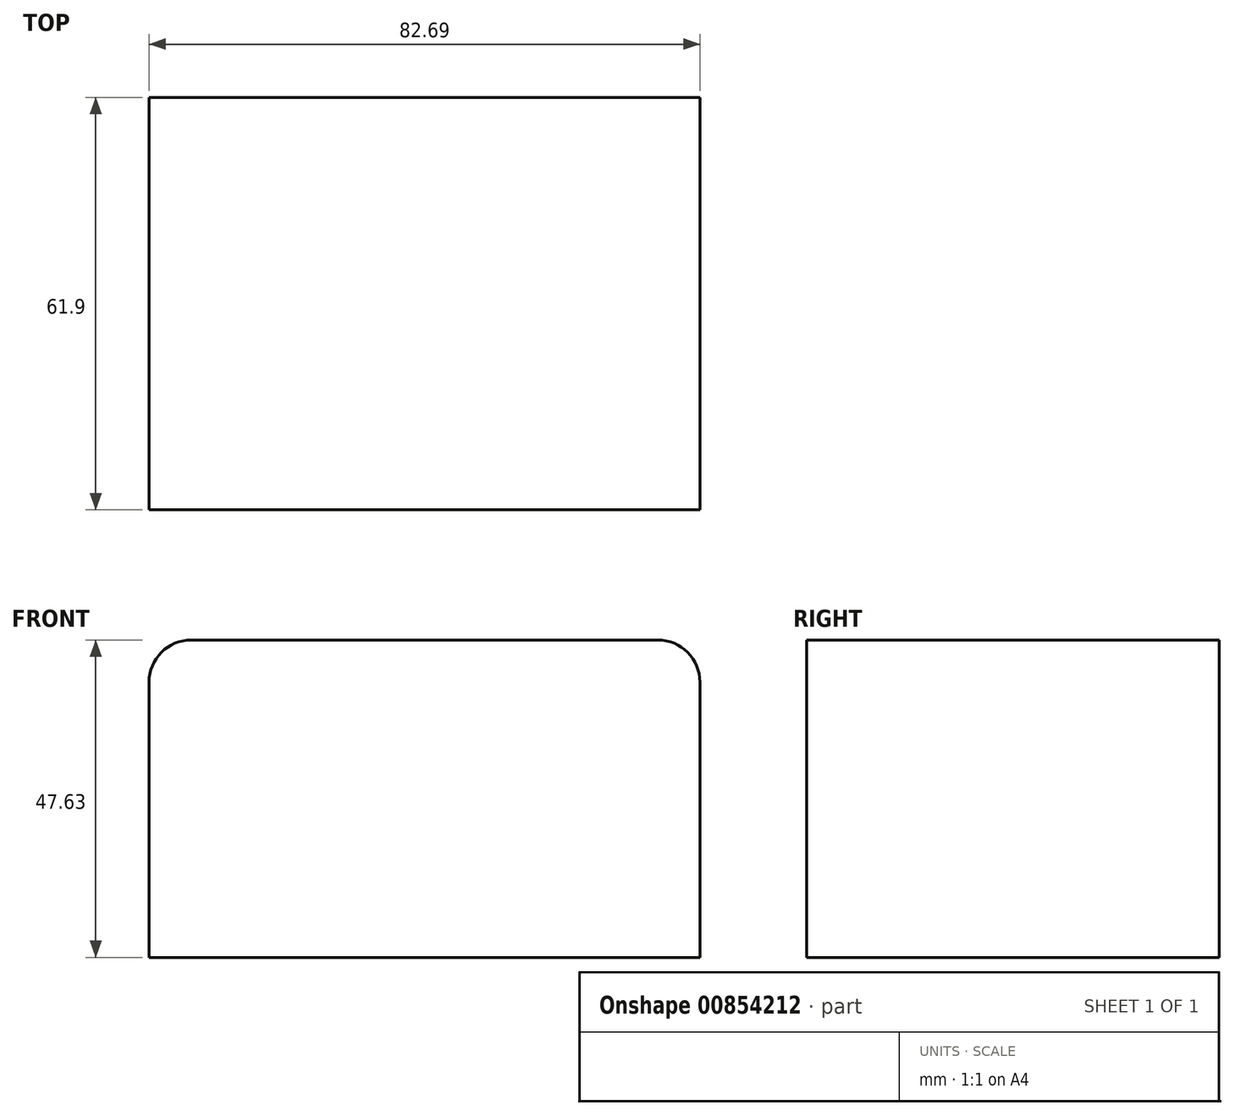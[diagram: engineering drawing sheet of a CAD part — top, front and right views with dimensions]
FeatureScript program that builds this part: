
annotation { "Feature Type Name" : "Feature", "Feature Type Description" : "" }
export const myFeature = defineFeature(function(context is Context, id is Id, definition is map)
    precondition{}
    {
        {
            var Q0;
            Q0=qCreatedBy(makeId("Front.planeOp"),FACE);
            var sketch = newSketch(context, id + "F0", { "sketchPlane" : qUnion([Q0])});
            skLineSegment(sketch, "E0.bottom", {"start": v(-35.5, 15.19) * mm, "end": v(47.18, 15.19) * mm});
            skLineSegment(sketch, "E0.top", {"start": v(-35.5, -32.44) * mm, "end": v(47.18, -32.44) * mm});
            skLineSegment(sketch, "E0.left", {"start": v(-35.5, 15.19) * mm, "end": v(-35.5, -32.44) * mm});
            skLineSegment(sketch, "E0.right", {"start": v(47.18, 15.19) * mm, "end": v(47.18, -32.44) * mm});
            skPoint(sketch, "E1.visualSharp", {"position": v(-35.5, 15.19) * mm});
            skPoint(sketch, "E2.visualSharp", {"position": v(47.18, 15.19) * mm});
            skSolve(sketch);
        }
        {
            var Q0;
            Q0 = qSketchRegion(id + "F0", true);
            extrude(context, id + "F1", {"entities" : qUnion([Q0]), "depth" : 61.9 * mm, "offsetDistance" : 25.4 * mm});
        }
        {
            var Q0;
            Q0=makeQuery(id+"F1.opExtrude","SWEPT_EDGE",EDGE,{"disambiguationData":[OSD([sQuery(id+"F0.wireOp",EDGE,"E0.bottom"),sQuery(id+"F0.wireOp",EDGE,"E0.right")])]});
            var Q1;
            Q1=makeQuery(id+"F1.opExtrude","SWEPT_EDGE",EDGE,{"disambiguationData":[OSD([sQuery(id+"F0.wireOp",EDGE,"E0.bottom"),sQuery(id+"F0.wireOp",EDGE,"E0.left")])]});
            fillet(context, id + "F2", {"entities" : qUnion([Q0, Q1]), "radius" : 6.35 * mm, "tangentPropagation" : true, "allowEdgeOverflow" : false});
        }
    });
